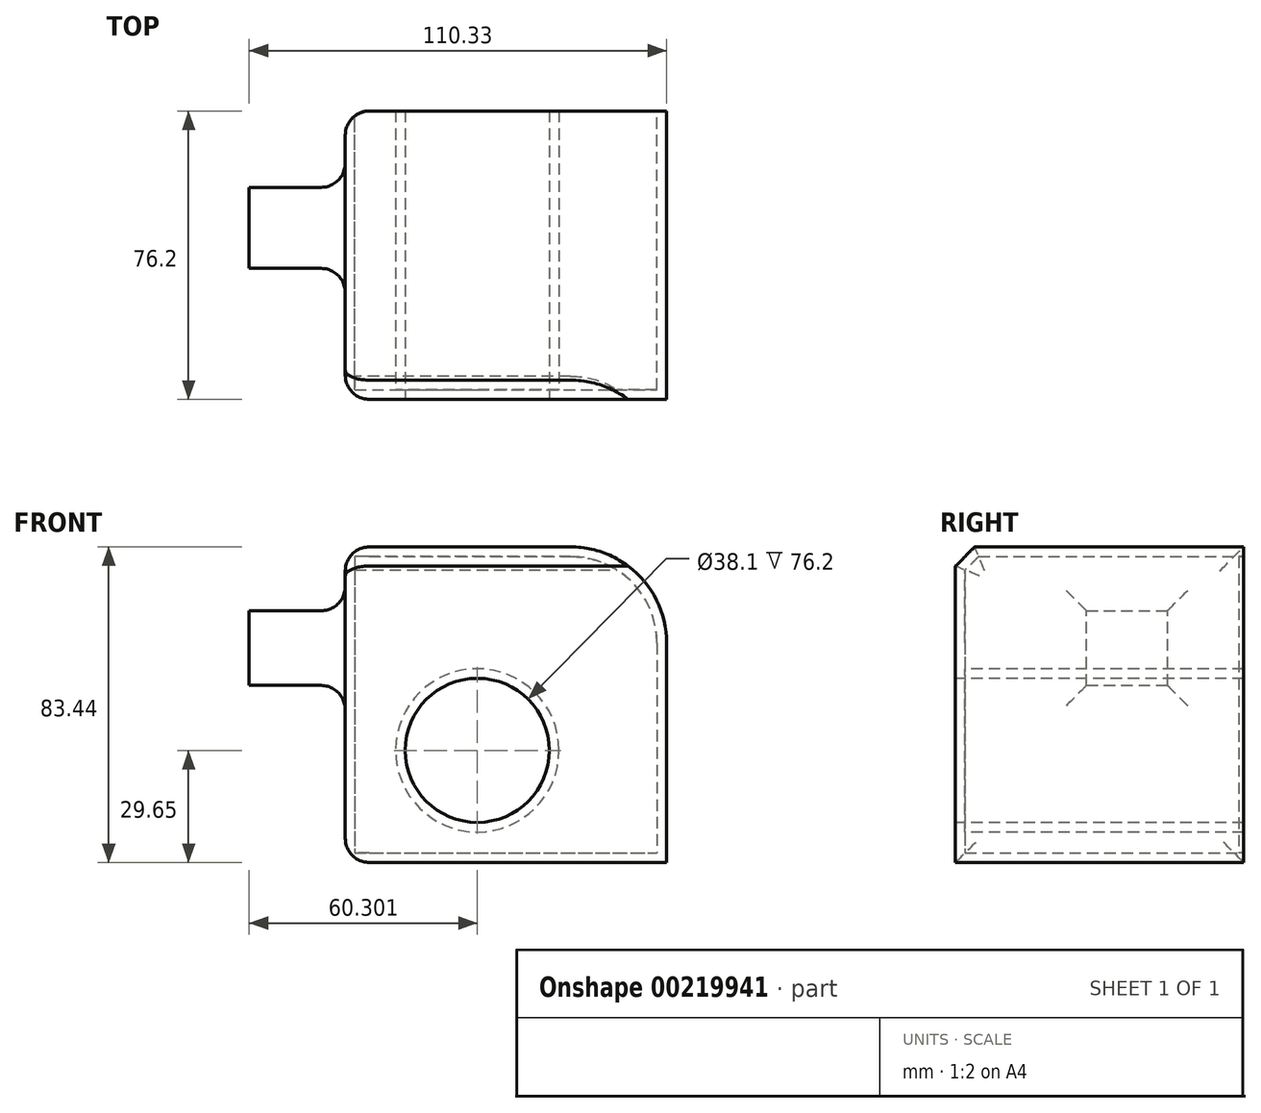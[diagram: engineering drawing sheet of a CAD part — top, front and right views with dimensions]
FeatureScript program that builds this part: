
annotation { "Feature Type Name" : "Feature", "Feature Type Description" : "" }
export const myFeature = defineFeature(function(context is Context, id is Id, definition is map)
    precondition{}
    {
        {
            var Q0;
            Q0=qCreatedBy(makeId("Front.planeOp"),FACE);
            var sketch = newSketch(context, id + "F0", { "sketchPlane" : qUnion([Q0])});
            skLineSegment(sketch, "E0.bottom", {"start": v(-45.9, 53.79) * mm, "end": v(39.04, 53.79) * mm});
            skLineSegment(sketch, "E0.top", {"start": v(-45.9, -29.65) * mm, "end": v(39.04, -29.65) * mm});
            skLineSegment(sketch, "E0.left", {"start": v(-45.9, 53.79) * mm, "end": v(-45.9, -29.65) * mm});
            skLineSegment(sketch, "E0.right", {"start": v(39.04, 53.79) * mm, "end": v(39.04, -29.65) * mm});
            skSolve(sketch);
        }
        {
            var Q0;
            Q0 = qSketchRegion(id + "F0", true);
            extrude(context, id + "F1", {"entities" : qUnion([Q0]), "depth" : 76.2 * mm});
        }
        {
            var Q0;
            Q0=makeQuery(id+"F1.opExtrude","CAP_EDGE",EDGE,{"disambiguationData":[OSD([sQuery(id+"F0.wireOp",EDGE,"E0.bottom")])],"isStart":false});
            chamfer(context, id + "F2", {"entities" : qUnion([Q0]), "width" : 5.08 * mm, "tangentPropagation" : true});
        }
        {
            var Q0;
            Q0=makeQuery(id+"F1.opExtrude","SWEPT_EDGE",EDGE,{"disambiguationData":[OSD([sQuery(id+"F0.wireOp",EDGE,"E0.bottom"),sQuery(id+"F0.wireOp",EDGE,"E0.right")])]});
            fillet(context, id + "F3", {"entities" : qUnion([Q0]), "radius" : 25.4 * mm, "tangentPropagation" : true, "allowEdgeOverflow" : false});
        }
        {
            var Q0;
            Q0=makeQuery(id+"F1.opExtrude","CAP_FACE",FACE,{"disambiguationData":[OSD([sQuery(id+"F0.wireOp",EDGE,"E0.bottom"),sQuery(id+"F0.wireOp",EDGE,"E0.top"),sQuery(id+"F0.wireOp",EDGE,"E0.left"),sQuery(id+"F0.wireOp",EDGE,"E0.right")])],"isStart":false});
            var sketch = newSketch(context, id + "F4", { "sketchPlane" : qUnion([Q0])});
            skCircle(sketch, "E1", {"center": v(-10.99, 0) * mm, "radius": 26.57 * mm});
            skSolve(sketch);
        }
        {
            var Q0;
            Q0=sQuery(id+"F4.wireOp",VERTEX,"E1.center");
            var Q1;
            Q1=makeQuery(id+"F1.opExtrude","SWEPT_BODY",BODY,{"disambiguationData":[OSD([sQuery(id+"F0.wireOp",EDGE,"E0.bottom"),sQuery(id+"F0.wireOp",EDGE,"E0.top"),sQuery(id+"F0.wireOp",EDGE,"E0.left"),sQuery(id+"F0.wireOp",EDGE,"E0.right")])]});
            hole(context, id + "F5", {"style" : HoleStyle.SIMPLE, "endStyle" : HoleEndStyle.THROUGH, "holeDiameter" : 38.1 * mm, "locations" : qUnion([Q0]), "scope" : qUnion([Q1]), "isTappedThrough" : true});
        }
        {
            var Q0;
            Q0=makeQuery(id+"F1.opExtrude","CAP_FACE",FACE,{"disambiguationData":[OSD([sQuery(id+"F0.wireOp",EDGE,"E0.bottom"),sQuery(id+"F0.wireOp",EDGE,"E0.top"),sQuery(id+"F0.wireOp",EDGE,"E0.left"),sQuery(id+"F0.wireOp",EDGE,"E0.right")])],"isStart":true});
            shell(context, id + "F8", {"entities" : qUnion([Q0]), "thickness" : 2.54 * mm});
        }
        {
            var Q0;
            Q0=makeQuery(id+"F1.opExtrude","SWEPT_FACE",FACE,{"disambiguationData":[OSD([sQuery(id+"F0.wireOp",EDGE,"E0.left")])]});
            var sketch = newSketch(context, id + "F9", { "sketchPlane" : qUnion([Q0])});
            skLineSegment(sketch, "E2.bottom", {"start": v(41.6, 17.15) * mm, "end": v(20.17, 17.15) * mm});
            skLineSegment(sketch, "E2.top", {"start": v(41.6, 36.91) * mm, "end": v(20.17, 36.91) * mm});
            skLineSegment(sketch, "E2.left", {"start": v(41.6, 17.15) * mm, "end": v(41.6, 36.91) * mm});
            skLineSegment(sketch, "E2.right", {"start": v(20.17, 17.15) * mm, "end": v(20.17, 36.91) * mm});
            skSolve(sketch);
        }
        {
            var Q0;
            Q0=makeQuery(id+"F9.imprint","IMPRINT",FACE,{"disambiguationData":[TD([[makeQuery(id+"F9.imprint","IMPRINT",EDGE,{"derivedFrom":sQuery(id+"F9.wireOp",EDGE,"E2.bottom")}),-1.0]])]});
            extrude(context, id + "F10", {"entities" : qUnion([Q0]), "operationType" : NewBodyOperationType.ADD, "depth" : 25.4 * mm});
        }
        {
            var Q0;
            Q0=makeQuery(id+"F1.opExtrude","SWEPT_FACE",FACE,{"disambiguationData":[OSD([sQuery(id+"F0.wireOp",EDGE,"E0.left")])]});
            fillet(context, id + "F11", {"entities" : qUnion([Q0]), "radius" : 6.35 * mm, "tangentPropagation" : true, "allowEdgeOverflow" : false});
        }
    });
